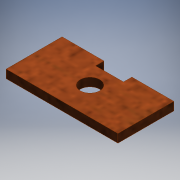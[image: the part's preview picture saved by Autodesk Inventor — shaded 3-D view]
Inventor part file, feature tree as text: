
AUTODESK INVENTOR PART (.ipt)
format: ipt  version: 2016 (Build 200138000, 138)  size: 121,344 bytes
history: native  units: mm
features: extrude x2, sketch x2, other x1
ambient origin geometry x8: Origin, YZ Plane, XZ Plane, XY Plane, X Axis, Y Axis, Z Axis, Center Point
bodies: Body1 (feature_tree)
feature tree (5):
  other  "Sólido1"
  extrude  "Extrusión1"  Depth=3.0mm
  extrude  "Extrusión2"  Depth=3.0mm TaperAngle=0.0deg
  sketch  "Boceto1"  dims[d0=3.0mm d1=0.0mm d3=5.0mm]
  sketch  "Boceto2"  dims[d4=5.0mm d5=3.0mm d6=0.0mm]
